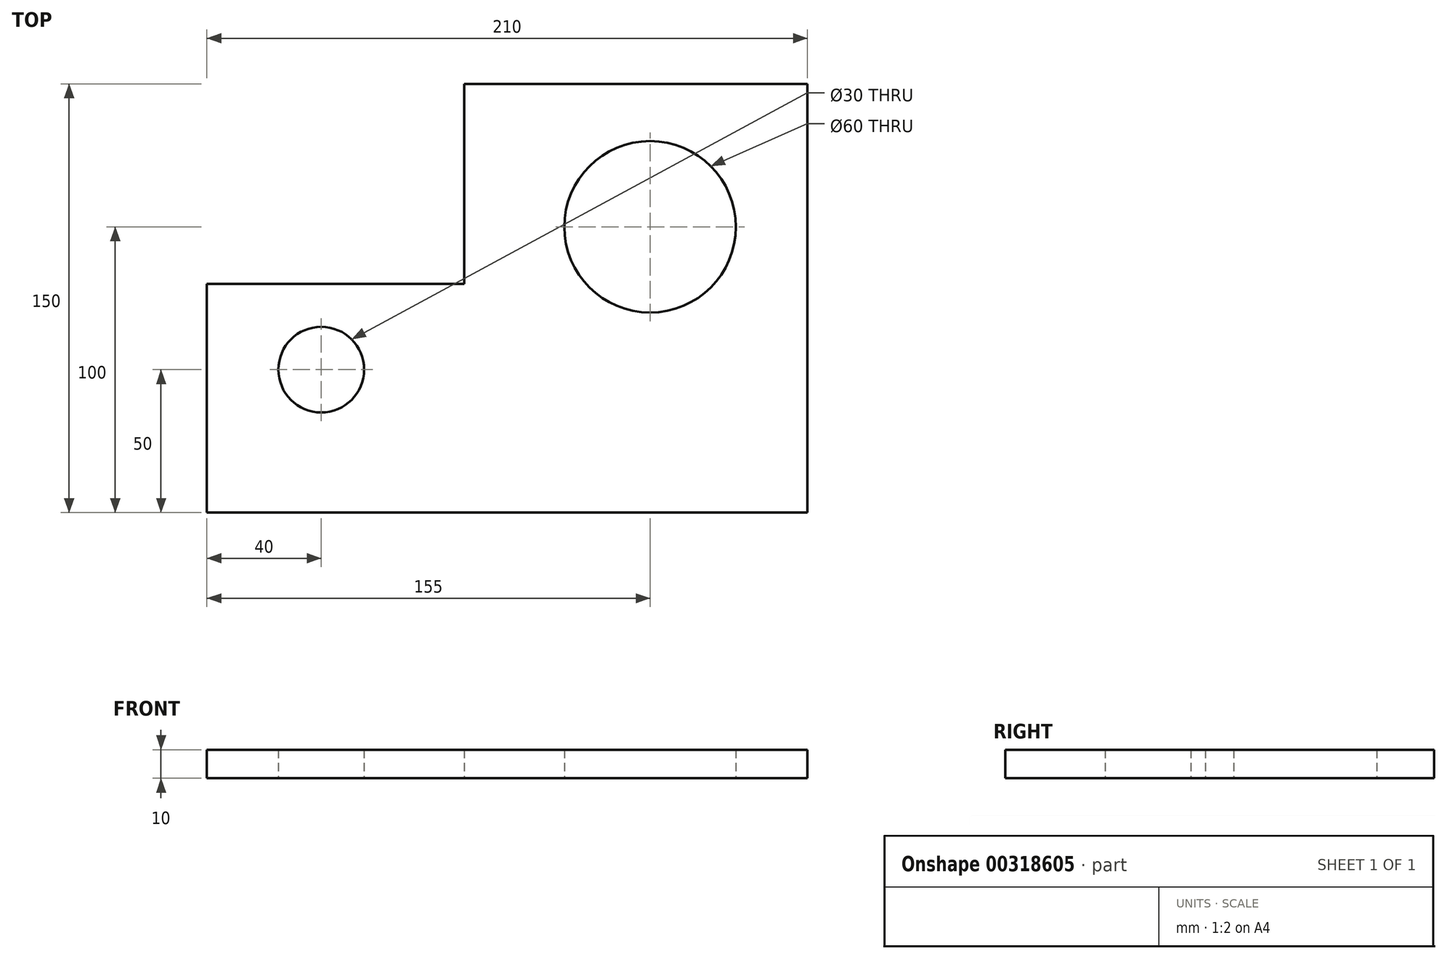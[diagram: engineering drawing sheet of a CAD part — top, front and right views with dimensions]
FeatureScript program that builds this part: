
annotation { "Feature Type Name" : "Feature", "Feature Type Description" : "" }
export const myFeature = defineFeature(function(context is Context, id is Id, definition is map)
    precondition{}
    {
        {
            var Q0;
            Q0=qCreatedBy(makeId("Top.planeOp"),FACE);
            var sketch = newSketch(context, id + "F0", { "sketchPlane" : qUnion([Q0])});
            skLineSegment(sketch, "E0", {"start": v(0, 0) * mm, "end": v(0, 150) * mm});
            skLineSegment(sketch, "E1", {"start": v(0, 150) * mm, "end": v(-120, 150) * mm});
            skLineSegment(sketch, "E2", {"start": v(-120, 150) * mm, "end": v(-120, 80) * mm});
            skLineSegment(sketch, "E3", {"start": v(-120, 80) * mm, "end": v(-210, 80) * mm});
            skLineSegment(sketch, "E4", {"start": v(-210, 80) * mm, "end": v(-210, 0) * mm});
            skLineSegment(sketch, "E5", {"start": v(-210, 0) * mm, "end": v(0, 0) * mm});
            skLineSegment(sketch, "E6", {"start": v(-170, 0) * mm, "end": v(-170, 50) * mm, "construction": true});
            skLineSegment(sketch, "E7", {"start": v(-170, 50) * mm, "end": v(-210, 50) * mm, "construction": true});
            skLineSegment(sketch, "E8", {"start": v(0, 100) * mm, "end": v(-55, 100) * mm, "construction": true});
            skLineSegment(sketch, "E9", {"start": v(-55, 100) * mm, "end": v(-55, 0) * mm, "construction": true});
            skCircle(sketch, "E10", {"center": v(-170, 50) * mm, "radius": 15 * mm});
            skCircle(sketch, "E11", {"center": v(-55, 100) * mm, "radius": 30 * mm});
            skSolve(sketch);
        }
        {
            var Q0;
            Q0=makeQuery(id+"F0.imprint","IMPRINT",FACE,{"disambiguationData":[TD([[makeQuery(id+"F0.imprint","IMPRINT",EDGE,{"derivedFrom":sQuery(id+"F0.wireOp",EDGE,"E0")}),1.0]])]});
            extrude(context, id + "F1", {"entities" : qUnion([Q0]), "depth" : 10 * mm});
        }
    });
